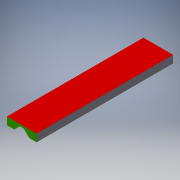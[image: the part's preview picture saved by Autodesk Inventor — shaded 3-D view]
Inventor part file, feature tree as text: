
AUTODESK INVENTOR PART (.ipt)
format: ipt  version: 2019 (Build 230136000, 136)  size: 242,176 bytes
history: native  units: in
note: dims shown in document units (in); Inventor stores cm internally (conversion verified against a paired STEP export)
features: extrude x7, sketch x7, projected_geometry x4, mirror x2, plane x1, pattern_linear x1
ambient origin geometry x8: Origin, YZ Plane, XZ Plane, XY Plane, X Axis, Y Axis, Z Axis, Center Point
bodies: Solid1 (feature_tree)
feature tree (22):
  extrude  "Extrusion1"  Depth=0.975in
  extrude  "Extrusion2"  TaperAngle=45.0deg  [1 undecoded]
  extrude  "Extrusion3"  Depth=0.125in
  plane  "Work Plane1"
  extrude  "Extrusion4"  Depth=0.25in TaperAngle=0.0deg
  mirror  "Mirror1"
  pattern_linear  "Rectangular Pattern1"  Spacing1=-1.3125in  [1 undecoded]
  extrude  "Extrusion5"  TaperAngle=150.0deg  [1 undecoded]
  extrude  "Extrusion6"  Depth=0.04in
  extrude  "Extrusion7"  Depth=0.125in
  mirror  "Mirror2"
  sketch  "Sketch1"  dims[d0=0.975in d1=4.5in]
  sketch  "Sketch2"  dims[d2=0.25in d3=0.0in d4=45.0deg]
  sketch  "Sketch3"  dims[d5=45.0deg d6=0.125in]
  sketch  "Sketch4"  dims[d7=0.185in d8=0.25in d9=0.0in]
  projected_geometry  "Projected Loop1"
  sketch  "Sketch6"  dims[d14=0.125in]
  projected_geometry  "Projected Loop2"
  sketch  "Sketch7"  dims[d15=2.25in]
  sketch  "Sketch8"  dims[d16=0.25in d17=0.0in d18=-1.3125in d19=150.0deg d20=0.04in d21=0.125in d22=0.125in d23=0.0in d27=0.7874in d29=1.875in d30=0.125in d31=0.125in d32=2.0in d33=0.0in d34=2.0in d35=0.0in d36=45.0deg d37=0.125in d38=0.125in d39=45.0deg d40=0.25in d41=2.0in d42=0.0in]
  projected_geometry  "Projected Loop3"
  projected_geometry  "Projected Loop4"
note: 3 required parameter values undecoded (feature->parameter linkage not recoverable at this tier; creation-order binding heuristic only, values carry confidence <= 0.55)
